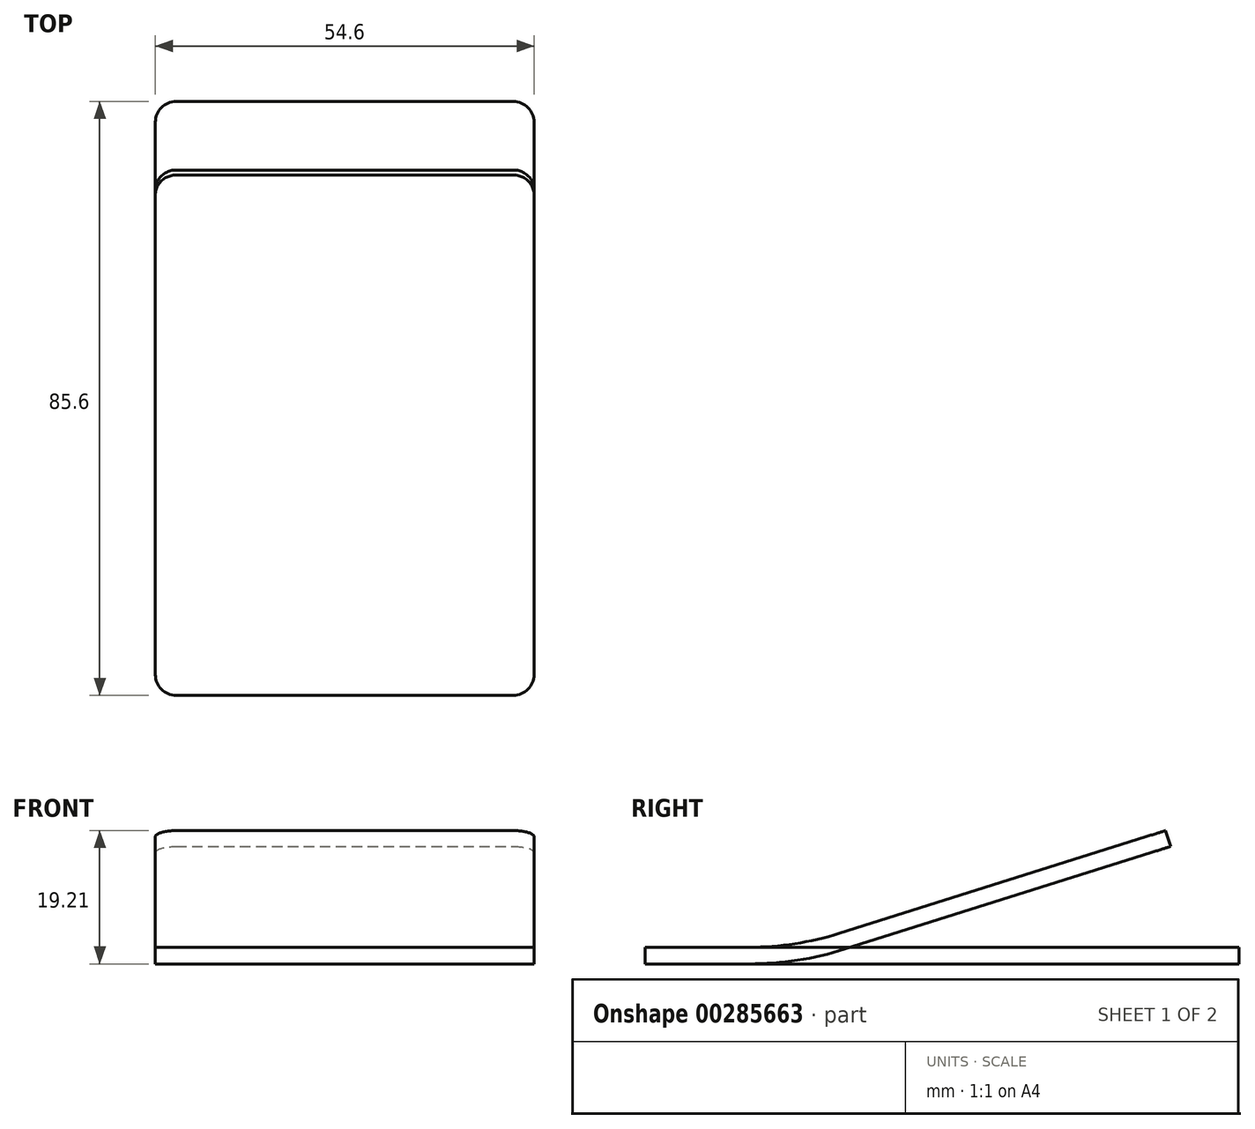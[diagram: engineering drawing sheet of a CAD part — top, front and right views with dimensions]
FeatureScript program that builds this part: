
annotation { "Feature Type Name" : "Feature", "Feature Type Description" : "" }
export const myFeature = defineFeature(function(context is Context, id is Id, definition is map)
    precondition{}
    {
        {
            var Q0;
            Q0=qCreatedBy(makeId("Top.planeOp"),FACE);
            var sketch = newSketch(context, id + "F0", { "sketchPlane" : qUnion([Q0])});
            skLineSegment(sketch, "E0.bottom", {"start": v(3, 85.6) * mm, "end": v(51.6, 85.6) * mm});
            skLineSegment(sketch, "E0.top", {"start": v(3, 0) * mm, "end": v(51.6, 0) * mm});
            skLineSegment(sketch, "E0.left", {"start": v(0, 82.6) * mm, "end": v(0, 3) * mm});
            skLineSegment(sketch, "E0.right", {"start": v(54.6, 82.6) * mm, "end": v(54.6, 3) * mm});
            skPoint(sketch, "E1.visualSharp", {"position": v(0, 85.6) * mm});
            skArc(sketch, "E1.filletArc", {"start": v(3, 85.6) * mm, "mid": v(0.88, 84.72) * mm, "end": v(0, 82.6) * mm});
            skPoint(sketch, "E2.visualSharp", {"position": v(54.6, 85.6) * mm});
            skArc(sketch, "E2.filletArc", {"start": v(54.6, 82.6) * mm, "mid": v(53.72, 84.72) * mm, "end": v(51.6, 85.6) * mm});
            skPoint(sketch, "E3.visualSharp", {"position": v(54.6, 0) * mm});
            skArc(sketch, "E3.filletArc", {"start": v(51.6, 0) * mm, "mid": v(53.72, 0.88) * mm, "end": v(54.6, 3) * mm});
            skPoint(sketch, "E4.visualSharp", {"position": v(0, 0) * mm});
            skArc(sketch, "E4.filletArc", {"start": v(0, 3) * mm, "mid": v(0.88, 0.88) * mm, "end": v(3, 0) * mm});
            skSolve(sketch);
        }
        {
            var Q0;
            Q0=qSketchRegion(id+"F0",true);
            extrude(context, id + "F1", {"entities" : qUnion([Q0]), "depth" : 2.4 * mm});
        }
        {
            var Q0;
            Q0=makeQuery(id+"F1.opExtrude","SWEPT_FACE",FACE,{"disambiguationData":[OSD([sQuery(id+"F0.wireOp",EDGE,"E0.top")])]});
            var sketch = newSketch(context, id + "F2", { "sketchPlane" : qUnion([Q0])});
            skLineSegment(sketch, "E5.bottom", {"start": v(0, 0) * mm, "end": v(54.6, 0) * mm});
            skLineSegment(sketch, "E5.top", {"start": v(0, 2.4) * mm, "end": v(54.6, 2.4) * mm});
            skLineSegment(sketch, "E5.left", {"start": v(0, 0) * mm, "end": v(0, 2.4) * mm});
            skLineSegment(sketch, "E5.right", {"start": v(54.6, 0) * mm, "end": v(54.6, 2.4) * mm});
            skPoint(sketch, "E6.0", {"position": v(54.6, 2.4) * mm});
            skSolve(sketch);
        }
        {
            var Q0;
            Q0=makeQuery(id+"F1.opExtrude","SWEPT_FACE",FACE,{"disambiguationData":[OSD([sQuery(id+"F0.wireOp",EDGE,"E0.right")])]});
            var sketch = newSketch(context, id + "F3", { "sketchPlane" : qUnion([Q0])});
            skLineSegment(sketch, "E7", {"start": v(0, 2.4) * mm, "end": v(15, 2.4) * mm});
            skArc(sketch, "E8.filletArc", {"start": v(15, 2.4) * mm, "mid": v(21.58, 2.9) * mm, "end": v(28, 4.4) * mm});
            skLineSegment(sketch, "E9", {"start": v(28, 4.4) * mm, "end": v(75, 19.21) * mm});
            skSolve(sketch);
        }
        {
            var Q0;
            Q0=qSketchRegion(id+"F2",true);
            var Q1;
            Q1=sQuery(id+"F3.wireOp",EDGE,"E7");
            var Q2;
            Q2=sQuery(id+"F3.wireOp",EDGE,"E8.filletArc");
            var Q3;
            Q3=sQuery(id+"F3.wireOp",EDGE,"E9");
            sweep(context, id + "F4", {"profiles" : qUnion([Q0]), "path" : qUnion([Q1, Q2, Q3])});
        }
        {
            var Q0;
            Q0=makeQuery(id+"F4.opSweep","CAP_EDGE",EDGE,{"disambiguationData":[OSD([sQuery(id+"F2.wireOp",EDGE,"E5.right"),sQuery(id+"F3.wireOp",VERTEX,"E7.start")])],"isStart":true});
            var Q1;
            Q1=makeQuery(id+"F4.opSweep","CAP_EDGE",EDGE,{"disambiguationData":[OSD([sQuery(id+"F2.wireOp",EDGE,"E5.left"),sQuery(id+"F3.wireOp",VERTEX,"E7.start")])],"isStart":true});
            var Q2;
            Q2=makeQuery(id+"F4.opSweep","CAP_EDGE",EDGE,{"disambiguationData":[OSD([sQuery(id+"F2.wireOp",EDGE,"E5.right"),sQuery(id+"F3.wireOp",VERTEX,"E9.end")])],"isStart":false});
            var Q3;
            Q3=makeQuery(id+"F4.opSweep","CAP_EDGE",EDGE,{"disambiguationData":[OSD([sQuery(id+"F2.wireOp",EDGE,"E5.left"),sQuery(id+"F3.wireOp",VERTEX,"E9.end")])],"isStart":false});
            fillet(context, id + "F5", {"entities" : qUnion([Q0, Q1, Q2, Q3]), "radius" : 3 * mm, "tangentPropagation" : true, "allowEdgeOverflow" : false});
        }
    });
